# Revit family: Faucet-Sensor _Operated-Acorn-SW000-F60
name_source: partatom
category: Plumbing Fixtures
revit_build: Autodesk Revit 2018 (Build: 20170223_1515(x64)
units: mm (PartAtom-declared; Revit-internal decimal feet)

## family parameters
Always vertical = No
Cut with Voids When Loaded = No
OmniClass Number = 23.45.55.14
OmniClass Title = Single Faucets
Part Type = Normal
Room Calculation Point = No
Round Connector Dimension = Use Diameter
Shared = Yes
Work Plane-Based = Yes

## types (1)
- SW000-F60
    Assembly Code = D2020300
    CW Connection = No
    CWFU = 1.5
    Default Elevation = 0"
    Description = Single Temp Sensor Faucet with Stainless Steel Spout and Stainless Steel Deck Plate
    Finish = Stainless Steel-Acorn-#4 Satin
    Flow Rate = 0.5 GPM(1.9 LPM)
    HW Connection = No
    HWFU = 1.5
    Height = 5 1/2"
    IAPMO Compliance = Product meets NSF and lead-free standards
    Installation Type = Deck Mounted
    Length = 4 7/8"
    Manufacturer = Acorn
    Material = Stainless Steel-Acorn-#4 Satin
    Model = SW000-F60
    Plate Length = 6 5/8"
    Plate Visibility = No
    Plate Width = 2 3/8"
    Price = Prices may vary. Please consult Manufacturer Representative for most up-to-date price list.
    Product Documentation Link = https://www.acorneng.com
    Product Page URL = https://www.acorneng.com
    Tempered Water Connection = Yes
    Tempered Water Connection Diameter = 1/2"
    Tempered Water Connection Radius = 1/4"
    Type Comments = Faucet and Plate are designed for 1-5/16”dia. single hole centered deck punching.
    URL = https://www.acorneng.com
    Vent Connection = No
    WFU = 0
    Waste Connection = No

## geometry (parser evidence)
native form markers: Sweep x2
no freeform markers — native parametric forms only
